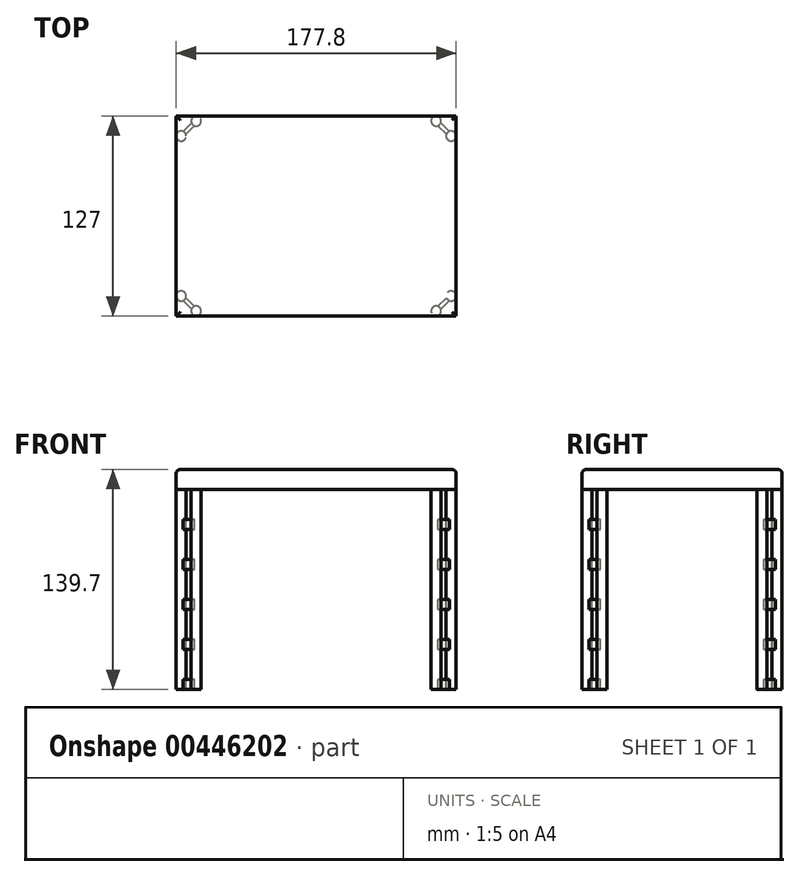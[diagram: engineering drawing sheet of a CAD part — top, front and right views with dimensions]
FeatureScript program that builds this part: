
annotation { "Feature Type Name" : "Feature", "Feature Type Description" : "" }
export const myFeature = defineFeature(function(context is Context, id is Id, definition is map)
    precondition{}
    {
        {
            var Q0;
            Q0=qCreatedBy(makeId("Top.planeOp"),FACE);
            var sketch = newSketch(context, id + "F0", { "sketchPlane" : qUnion([Q0])});
            skLineSegment(sketch, "E0.bottom", {"start": v(88.9, -63.5) * mm, "end": v(-88.9, -63.5) * mm});
            skLineSegment(sketch, "E0.top", {"start": v(88.9, 63.5) * mm, "end": v(-88.9, 63.5) * mm});
            skLineSegment(sketch, "E0.left", {"start": v(88.9, -63.5) * mm, "end": v(88.9, 63.5) * mm});
            skLineSegment(sketch, "E0.right", {"start": v(-88.9, -63.5) * mm, "end": v(-88.9, 63.5) * mm});
            skPoint(sketch, "E0.middle", {"position": v(0, 0) * mm});
            skSolve(sketch);
        }
        {
            var Q0;
            Q0=makeQuery(id+"F0.imprint","IMPRINT",FACE,{"disambiguationData":[TD([[makeQuery(id+"F0.imprint","IMPRINT",EDGE,{"derivedFrom":sQuery(id+"F0.wireOp",EDGE,"E0.bottom")}),-1.0]])]});
            extrude(context, id + "F1", {"entities" : qUnion([Q0]), "depth" : 12.7 * mm});
        }
        {
            var Q0;
            Q0=qCreatedBy(makeId("Top.planeOp"),FACE);
            var sketch = newSketch(context, id + "F2", { "sketchPlane" : qUnion([Q0])});
            skCircle(sketch, "E1", {"center": v(76.2, -60.33) * mm, "radius": 3.18 * mm});
            skCircle(sketch, "E2", {"center": v(85.73, -50.8) * mm, "radius": 3.18 * mm});
            skSolve(sketch);
        }
        {
            var Q0;
            Q0 = qSketchRegion(id + "F2", true);
            extrude(context, id + "F3", {"entities" : qUnion([Q0]), "operationType" : NewBodyOperationType.ADD, "oppositeDirection" : true, "depth" : 127 * mm});
        }
        {
            var Q0;
            Q0=qCreatedBy(makeId("Top.planeOp"),FACE);
            var sketch = newSketch(context, id + "F4", { "sketchPlane" : qUnion([Q0])});
            skCircle(sketch, "E3.0", {"center": v(76.2, -60.33) * mm, "radius": 3.18 * mm});
            skCircle(sketch, "E4.0", {"center": v(85.73, -50.8) * mm, "radius": 3.18 * mm});
            skLineSegment(sketch, "E5", {"start": v(76.2, -60.33) * mm, "end": v(85.73, -50.8) * mm});
            skSolve(sketch);
        }
        {
            var Q0;
            Q0=sQuery(id+"F4.wireOp",EDGE,"E5");
            var Q1;
            Q1=makeQuery(id+"F3.opExtrude","SWEPT_FACE",FACE,{"disambiguationData":[OSD([sQuery(id+"F2.wireOp",EDGE,"E2")])]});
            cPlane(context, id + "F5", {"entities" : qUnion([Q0, Q1]), "cplaneType" : CPlaneType.LINE_ANGLE, "offset" : 25.4 * mm, "angle" : 0 * degree, "width" : 152.4 * mm, "height" : 152.4 * mm});
        }
        {
            var Q0;
            Q0=qCreatedBy(id+"F5.planeOp",FACE);
            var sketch = newSketch(context, id + "F6", { "sketchPlane" : qUnion([Q0])});
            skLineSegment(sketch, "E6", {"start": v(27.87, 0) * mm, "end": v(27.87, -127) * mm});
            skLineSegment(sketch, "E7", {"start": v(24.7, -127) * mm, "end": v(24.7, -120.65) * mm});
            skLineSegment(sketch, "E8", {"start": v(11.23, -19.05) * mm, "end": v(11.23, -25.4) * mm});
            skPoint(sketch, "E9.orphan", {"position": v(8.05, -127) * mm});
            skPoint(sketch, "E10.orphan", {"position": v(27.87, -127) * mm});
            skPoint(sketch, "E11.orphan", {"position": v(8.05, 0) * mm});
            skPoint(sketch, "E12.orphan", {"position": v(27.87, 0) * mm});
            skPoint(sketch, "E13.0.start.orphan", {"position": v(21.52, -127) * mm});
            skPoint(sketch, "E14.0.end.orphan", {"position": v(14.4, -127) * mm});
            skLineSegment(sketch, "E15.bottom", {"start": v(24.7, -127) * mm, "end": v(11.23, -127) * mm});
            skLineSegment(sketch, "E15.top", {"start": v(24.7, -120.65) * mm, "end": v(11.23, -120.65) * mm});
            skLineSegment(sketch, "E15.right", {"start": v(11.23, -127) * mm, "end": v(11.23, -120.65) * mm});
            skLineSegment(sketch, "E16.bottom", {"start": v(24.7, -101.6) * mm, "end": v(11.23, -101.6) * mm});
            skLineSegment(sketch, "E16.top", {"start": v(24.7, -95.25) * mm, "end": v(11.23, -95.25) * mm});
            skLineSegment(sketch, "E16.left", {"start": v(24.7, -101.6) * mm, "end": v(24.7, -95.25) * mm});
            skLineSegment(sketch, "E16.right", {"start": v(11.23, -101.6) * mm, "end": v(11.23, -95.25) * mm});
            skLineSegment(sketch, "E17.bottom", {"start": v(24.7, -76.2) * mm, "end": v(11.23, -76.2) * mm});
            skLineSegment(sketch, "E17.top", {"start": v(24.7, -69.85) * mm, "end": v(11.23, -69.85) * mm});
            skLineSegment(sketch, "E17.left", {"start": v(24.7, -76.2) * mm, "end": v(24.7, -69.85) * mm});
            skLineSegment(sketch, "E17.right", {"start": v(11.23, -76.2) * mm, "end": v(11.23, -69.85) * mm});
            skLineSegment(sketch, "E18.right", {"start": v(11.23, -69.87) * mm, "end": v(11.23, -69.85) * mm});
            skLineSegment(sketch, "E19.bottom", {"start": v(24.7, -50.8) * mm, "end": v(11.23, -50.8) * mm});
            skLineSegment(sketch, "E19.top", {"start": v(24.7, -44.45) * mm, "end": v(11.23, -44.45) * mm});
            skLineSegment(sketch, "E19.left", {"start": v(24.7, -50.8) * mm, "end": v(24.7, -44.45) * mm});
            skLineSegment(sketch, "E19.right", {"start": v(11.23, -50.8) * mm, "end": v(11.23, -44.45) * mm});
            skLineSegment(sketch, "E20.bottom", {"start": v(24.7, -25.4) * mm, "end": v(11.23, -25.4) * mm});
            skLineSegment(sketch, "E20.top", {"start": v(24.7, -19.05) * mm, "end": v(11.23, -19.05) * mm});
            skLineSegment(sketch, "E20.left", {"start": v(24.7, -25.4) * mm, "end": v(24.7, -19.05) * mm});
            skLineSegment(sketch, "E20.right", {"start": v(11.23, -25.4) * mm, "end": v(11.23, -19.05) * mm});
            skLineSegment(sketch, "E21.trimOffspring", {"start": v(11.23, -120.65) * mm, "end": v(11.23, -127) * mm});
            skLineSegment(sketch, "E22.trimOffspring", {"start": v(11.23, -95.25) * mm, "end": v(11.23, -101.6) * mm});
            skLineSegment(sketch, "E23.trimOffspring", {"start": v(11.23, -69.85) * mm, "end": v(11.23, -76.2) * mm});
            skPoint(sketch, "E24.orphan", {"position": v(11.23, -63.5) * mm});
            skLineSegment(sketch, "E25.trimOffspring", {"start": v(11.23, -44.45) * mm, "end": v(11.23, -50.8) * mm});
            skPoint(sketch, "E26.0.end.orphan", {"position": v(24.7, 0) * mm});
            skPoint(sketch, "E26.0.start.orphan", {"position": v(21.52, 0) * mm});
            skPoint(sketch, "E27.0.end.orphan", {"position": v(14.4, 0) * mm});
            skPoint(sketch, "E27.0.start.orphan", {"position": v(11.23, 0) * mm});
            skSolve(sketch);
        }
        {
            var Q0;
            Q0=makeQuery(id+"F6.imprint","IMPRINT",FACE,{"disambiguationData":[TD([[makeQuery(id+"F6.imprint","IMPRINT",EDGE,{"derivedFrom":sQuery(id+"F6.wireOp",EDGE,"E20.bottom")}),-1.0]])]});
            var Q1;
            Q1=makeQuery(id+"F6.imprint","IMPRINT",FACE,{"disambiguationData":[TD([[makeQuery(id+"F6.imprint","IMPRINT",EDGE,{"derivedFrom":sQuery(id+"F6.wireOp",EDGE,"E19.bottom")}),-1.0]])]});
            var Q2;
            Q2=makeQuery(id+"F6.imprint","IMPRINT",FACE,{"disambiguationData":[TD([[makeQuery(id+"F6.imprint","IMPRINT",EDGE,{"derivedFrom":sQuery(id+"F6.wireOp",EDGE,"E17.bottom")}),-1.0]])]});
            var Q3;
            Q3=makeQuery(id+"F6.imprint","IMPRINT",FACE,{"disambiguationData":[TD([[makeQuery(id+"F6.imprint","IMPRINT",EDGE,{"derivedFrom":sQuery(id+"F6.wireOp",EDGE,"E16.bottom")}),-1.0]])]});
            var Q4;
            Q4=makeQuery(id+"F6.imprint","IMPRINT",FACE,{"disambiguationData":[TD([[makeQuery(id+"F6.imprint","IMPRINT",EDGE,{"derivedFrom":sQuery(id+"F6.wireOp",EDGE,"E15.bottom")}),-1.0]])]});
            extrude(context, id + "F7", {"entities" : qUnion([Q0, Q1, Q2, Q3, Q4]), "operationType" : NewBodyOperationType.ADD, "endBound" : BoundingType.SYMMETRIC, "depth" : 2.54 * mm});
        }
        {
            var Q0;
            Q0=makeQuery(id+"F1.opExtrude","CAP_FACE",FACE,{"disambiguationData":[OSD([sQuery(id+"F0.wireOp",EDGE,"E0.bottom"),sQuery(id+"F0.wireOp",EDGE,"E0.top"),sQuery(id+"F0.wireOp",EDGE,"E0.left"),sQuery(id+"F0.wireOp",EDGE,"E0.right")])],"isStart":false});
            fillet(context, id + "F8", {"entities" : qUnion([Q0]), "radius" : 2.54 * mm, "tangentPropagation" : true, "allowEdgeOverflow" : false});
        }
        {
            var Q0;
            {var subQ0=sQuery(id+"F0.wireOp",EDGE,"E0.bottom");var subQ1=sQuery(id+"F0.wireOp",EDGE,"E0.right");Q0=makeQuery(id+"F3.boolean.opBoolean","SPLIT",EDGE,{"disambiguationData":[TD([makeQuery(id+"F1.opExtrude","SWEPT_FACE",FACE,{"disambiguationData":[OSD([subQ1])]})])],"derivedFrom":makeQuery(id+"F1.opExtrude","CAP_EDGE",EDGE,{"disambiguationData":[OSD([subQ0])],"isStart":true})});}
            var Q1;
            {var subQ0=sQuery(id+"F0.wireOp",EDGE,"E0.bottom");var subQ1=sQuery(id+"F0.wireOp",EDGE,"E0.left");Q1=makeQuery(id+"F3.boolean.opBoolean","SPLIT",EDGE,{"disambiguationData":[TD([makeQuery(id+"F1.opExtrude","SWEPT_FACE",FACE,{"disambiguationData":[OSD([subQ0])]})])],"derivedFrom":makeQuery(id+"F1.opExtrude","CAP_EDGE",EDGE,{"disambiguationData":[OSD([subQ1])],"isStart":true})});}
            var Q2;
            Q2=makeQuery(id+"F1.opExtrude","SWEPT_EDGE",EDGE,{"disambiguationData":[OSD([sQuery(id+"F0.wireOp",EDGE,"E0.bottom"),sQuery(id+"F0.wireOp",EDGE,"E0.left")])]});
            fillet(context, id + "F9", {"entities" : qUnion([Q0, Q1, Q2]), "radius" : 2.54 * mm, "tangentPropagation" : true, "allowEdgeOverflow" : false});
        }
        {
            var Q0;
            Q0=makeQuery(id+"F1.opExtrude","SWEPT_BODY",BODY,{"disambiguationData":[OSD([sQuery(id+"F0.wireOp",EDGE,"E0.bottom"),sQuery(id+"F0.wireOp",EDGE,"E0.top"),sQuery(id+"F0.wireOp",EDGE,"E0.left"),sQuery(id+"F0.wireOp",EDGE,"E0.right")])]});
            var Q1;
            Q1=qCreatedBy(makeId("Right.planeOp"),FACE);
            mirror(context, id + "F10", {"operationType" : NewBodyOperationType.ADD, "entities" : qUnion([Q0]), "mirrorPlane" : qUnion([Q1])});
        }
        {
            var Q0;
            Q0=makeQuery(id+"F1.opExtrude","SWEPT_BODY",BODY,{"disambiguationData":[OSD([sQuery(id+"F0.wireOp",EDGE,"E0.bottom"),sQuery(id+"F0.wireOp",EDGE,"E0.top"),sQuery(id+"F0.wireOp",EDGE,"E0.left"),sQuery(id+"F0.wireOp",EDGE,"E0.right")])]});
            var Q1;
            Q1=qCreatedBy(makeId("Front.planeOp"),FACE);
            mirror(context, id + "F11", {"operationType" : NewBodyOperationType.ADD, "entities" : qUnion([Q0]), "mirrorPlane" : qUnion([Q1])});
        }
    });
